FCSTD DOCUMENT  (FreeCAD 0.16R6706 (Git))
Label: femur
License: All rights reserved
LicenseURL: http://en.wikipedia.org/wiki/All_rights_reserved
objects: Sketcher::SketchObject×3
note: 3 computed .brp shape members not serialized (recipe doc carries the construction recipe); baked Part::Feature solids carry a one-line shape summary decoded from their .brp

FEATURE [Sketcher::SketchObject] Sketch003  label="femur_down"
  sketch-geometry (38):
    g0: LineSegment [constr] StartX=-11.4129 StartY=31.5472 StartZ=0 EndX=48.5871 EndY=31.5472 EndZ=0
    g1: GeomPoint [constr] X=-11.4129 Y=31.5472 Z=0
    g2: GeomPoint [constr] X=48.5871 Y=31.5472 Z=0
    g3: GeomPoint [constr] X=18.5871 Y=31.5472 Z=0
    g4: LineSegment [constr] StartX=18.5871 StartY=37.0472 StartZ=0 EndX=18.5871 EndY=26.0472 EndZ=0
    g5: LineSegment [constr] StartX=-11.4129 StartY=37.0472 StartZ=0 EndX=48.5871 EndY=37.0472 EndZ=0
    g6: LineSegment [constr] StartX=-11.4129 StartY=26.0472 StartZ=0 EndX=48.5871 EndY=26.0472 EndZ=0
    g7: Circle CenterX=48.5871 CenterY=31.5472 CenterZ=0 NormalX=0 NormalY=0 NormalZ=1 Radius=1.5
    g8: Circle CenterX=-11.4129 CenterY=31.5472 CenterZ=0 NormalX=0 NormalY=0 NormalZ=1 Radius=1.5
    g9: ArcOfCircle CenterX=48.5871 CenterY=31.5472 CenterZ=0 NormalX=0 NormalY=0 NormalZ=1 Radius=5.5 StartAngle=4.71238 EndAngle=7.85399
    g10: ArcOfCircle CenterX=-11.4129 CenterY=31.5472 CenterZ=0 NormalX=0 NormalY=0 NormalZ=1 Radius=5.5 StartAngle=1.57079 EndAngle=4.71239
    g11: LineSegment StartX=48.5871 StartY=37.0472 StartZ=0 EndX=25.858 EndY=37.0472 EndZ=0
    g12: LineSegment [constr] StartX=22.1954 StartY=37.0472 StartZ=0 EndX=29.3838 EndY=26.7835 EndZ=0
    g13: LineSegment StartX=33.5621 StartY=26.0472 StartZ=0 EndX=31.8411 EndY=28.5045 EndZ=0
    g14: LineSegment StartX=29.3838 StartY=26.7835 StartZ=0 EndX=31.8411 EndY=28.5045 EndZ=0
    g15: LineSegment StartX=48.5871 StartY=26.0472 StartZ=0 EndX=33.5621 EndY=26.0472 EndZ=0
    g16: GeomPoint [constr] X=22.1954 Y=37.0472 Z=0
    g17: LineSegment StartX=23.9164 StartY=34.5899 StartZ=0 EndX=26.3737 EndY=36.3109 EndZ=0
    g18: LineSegment StartX=-11.4129 StartY=26.0472 StartZ=0 EndX=3.61207 EndY=26.0472 EndZ=0
    g19: LineSegment StartX=29.3838 StartY=26.7835 StartZ=0 EndX=29.8995 EndY=26.0472 EndZ=0
    g20: LineSegment StartX=26.3737 StartY=36.3109 StartZ=0 EndX=25.858 EndY=37.0472 EndZ=0
    g21: LineSegment [constr] StartX=14.9788 StartY=37.0472 StartZ=0 EndX=7.27468 EndY=26.0472 EndZ=0
    g22: LineSegment StartX=13.2578 StartY=34.5899 StartZ=0 EndX=10.8005 EndY=36.3109 EndZ=0
    g23: LineSegment StartX=10.8005 StartY=36.3109 StartZ=0 EndX=11.3162 EndY=37.0472 EndZ=0
    g24: LineSegment StartX=-11.4129 StartY=37.0472 StartZ=0 EndX=11.3162 EndY=37.0472 EndZ=0
    g25: LineSegment StartX=7.27468 StartY=26.0472 StartZ=0 EndX=7.79034 EndY=26.7835 EndZ=0
    g26: LineSegment StartX=7.79034 StartY=26.7835 StartZ=0 EndX=5.33307 EndY=28.5045 EndZ=0
    g27: LineSegment StartX=5.33307 StartY=28.5045 StartZ=0 EndX=3.61207 EndY=26.0472 EndZ=0
    g28: LineSegment StartX=29.8995 StartY=26.0472 StartZ=0 EndX=7.27468 EndY=26.0472 EndZ=0
    g29: LineSegment StartX=23.9164 StartY=34.5899 StartZ=0 EndX=22.1954 EndY=37.0472 EndZ=0
    g30: LineSegment StartX=13.2578 StartY=34.5899 StartZ=0 EndX=14.9788 EndY=37.0472 EndZ=0
    g31: LineSegment StartX=14.9788 StartY=37.0472 StartZ=0 EndX=22.1954 EndY=37.0472 EndZ=0
    g32: LineSegment [constr] StartX=22.1954 StartY=37.0472 StartZ=0 EndX=24.6527 EndY=38.7682 EndZ=0
    g33: LineSegment [constr] StartX=25.858 StartY=37.0472 StartZ=0 EndX=24.6527 EndY=38.7682 EndZ=0
    g34: LineSegment [constr] StartX=14.9788 StartY=37.0472 StartZ=0 EndX=12.5215 EndY=38.7682 EndZ=0
    g35: LineSegment [constr] StartX=11.3162 StartY=37.0472 StartZ=0 EndX=12.5215 EndY=38.7682 EndZ=0
    g36: Circle CenterX=18.5871 CenterY=31.5472 CenterZ=0 NormalX=0 NormalY=0 NormalZ=1 Radius=1.2
    g37: LineSegment [constr] StartX=18.5871 StartY=34.5899 StartZ=0 EndX=18.5871 EndY=26.7835 EndZ=0
  constraints (99):
    c: PointOnObject(g1,g0)
    c: PointOnObject(g2,g0)
    c: Symmetric(g1,g2,g3)
    c: Distance(g3,g2) = 30
    c: Vertical(g4)
    c: Symmetric(g4,g4,g3)
    c: Distance(g3,g4) = 5.5
    c: Horizontal(g5)
    c: PointOnObject(g4,g5)
    c: Horizontal(g6)
    c: PointOnObject(g4,g6)
    c: Coincident(g7,g2)
    c: Radius(g7) = 1.5
    c: Coincident(g8,g1)
    c: Radius(g8) = 1.5
    c: Coincident(g9,g2)
    c: Coincident(g9,g6)
    c: Coincident(g5,g9)
    c: Tangent(g9,g5)
    c: Coincident(g10,g1)
    c: Coincident(g10,g6)
    c: Tangent(g6,g10)
    c: Coincident(g5,g10)
    c: Coincident(g11,g5)
    c: Coincident(g0,g2)
    c: Coincident(g0,g1)
    c: PointOnObject(g14,g12)
    c: Distance(g13,g13) = 3
    c: Coincident(g14,g13)
    c: Coincident(g15,g6)
    c: Perpendicular(g14,g12)
    c: Perpendicular(g14,g13)
    c: Distance(g13,g12) = 3
    c: PointOnObject(g17,g12)
    c: Distance(g17,g16) = 3
    c: Distance(g17,g17) = 3
    c: Perpendicular(g12,g17)
    c: PointOnObject(g12,g14)
    c: Coincident(g18,g6)
    c: PointOnObject(g13,g6)
    c: Coincident(g15,g13)
    c: Coincident(g19,g12)
    c: PointOnObject(g19,g6)
    c: Perpendicular(g14,g19)
    c: Coincident(g20,g17)
    c: PointOnObject(g20,g5)
    c: Perpendicular(g17,g20)
    c: Coincident(g11,g20)
    c: PointOnObject(g21,g6)
    c: PointOnObject(g22,g21)
    c: Distance(g22,g21) = 3
    c: Distance(g22,g22) = 3
    c: Perpendicular(g21,g22)
    c: Coincident(g23,g22)
    c: PointOnObject(g23,g5)
    c: Perpendicular(g22,g23)
    c: Coincident(g24,g5)
    c: Coincident(g23,g24)
    c: Coincident(g25,g21)
    c: PointOnObject(g25,g21)
    c: Coincident(g26,g25)
    c: Distance(g26,g25) = 3
    c: Coincident(g27,g26)
    c: PointOnObject(g27,g6)
    c: Distance(g27,g26) = 3
    c: Perpendicular(g26,g27)
    c: Perpendicular(g21,g26)
    c: Coincident(g18,g27)
    c: Coincident(g28,g19)
    c: Coincident(g21,g28)
    c: Coincident(g29,g12)
    c: Coincident(g17,g29)
    c: Coincident(g16,g12)
    c: PointOnObject(g12,g5)
    c: PointOnObject(g21,g5)
    c: Coincident(g30,g22)
    c: Coincident(g21,g30)
    c: Coincident(g31,g21)
    c: Coincident(g12,g31)
    c: Distance(g13,g0) = 16
    c: Tangent(g6,g9)
    c: Coincident(g32,g12)
    c: Perpendicular(g32,g12)
    c: Coincident(g33,g11)
    c: Parallel(g20,g33)
    c: Coincident(g32,g33)
    c: Distance(g32,g0) = 25
    c: Coincident(g34,g21)
    c: Perpendicular(g21,g34)
    c: Coincident(g35,g23)
    c: Parallel(g35,g23)
    c: Coincident(g34,g35)
    c: Distance(g18,g0) = 16
    c: Distance(g34,g0) = 25
    c: Radius(g36) = 1.2
    c: Symmetric(g25,g12,g37)
    c: Symmetric(g22,g17,g37)
    c: PointOnObject(g36,g37)
    c: PointOnObject(g36,g0)
FEATURE [Sketcher::SketchObject] Sketch004  label="femur_up"
  sketch-geometry (52):
    g0: LineSegment [constr] StartX=-9.22309 StartY=9.62854 StartZ=0 EndX=50.7769 EndY=9.62854 EndZ=0
    g1: GeomPoint [constr] X=-9.22309 Y=9.62854 Z=0
    g2: GeomPoint [constr] X=50.7769 Y=9.62854 Z=0
    g3: GeomPoint [constr] X=20.7769 Y=9.62854 Z=0
    g4: LineSegment [constr] StartX=20.7769 StartY=15.1285 StartZ=0 EndX=20.7769 EndY=4.12854 EndZ=0
    g5: LineSegment [constr] StartX=-9.22309 StartY=15.1285 StartZ=0 EndX=50.7769 EndY=15.1285 EndZ=0
    g6: LineSegment [constr] StartX=-9.22309 StartY=4.12854 StartZ=0 EndX=50.7769 EndY=4.12854 EndZ=0
    g7: Circle CenterX=50.7769 CenterY=9.62854 CenterZ=0 NormalX=0 NormalY=0 NormalZ=1 Radius=3.5
    g8: Circle CenterX=-9.22309 CenterY=9.62854 CenterZ=0 NormalX=0 NormalY=0 NormalZ=1 Radius=3.5
    g9: LineSegment StartX=50.7769 StartY=15.1285 StartZ=0 EndX=28.0478 EndY=15.1285 EndZ=0
    g10: LineSegment [constr] StartX=24.3852 StartY=15.1285 StartZ=0 EndX=31.5737 EndY=4.8648 EndZ=0
    g11: LineSegment StartX=35.7519 StartY=4.12854 StartZ=0 EndX=34.0309 EndY=6.5858 EndZ=0
    g12: LineSegment StartX=31.5737 StartY=4.8648 StartZ=0 EndX=34.0309 EndY=6.5858 EndZ=0
    g13: LineSegment StartX=50.7769 StartY=4.12854 StartZ=0 EndX=35.7519 EndY=4.12854 EndZ=0
    g14: GeomPoint [constr] X=24.3852 Y=15.1285 Z=0
    g15: LineSegment StartX=26.1062 StartY=12.6713 StartZ=0 EndX=28.5635 EndY=14.3923 EndZ=0
    g16: LineSegment StartX=-9.22309 StartY=4.12854 StartZ=0 EndX=5.80189 EndY=4.12854 EndZ=0
    g17: LineSegment StartX=31.5737 StartY=4.8648 StartZ=0 EndX=32.0893 EndY=4.12854 EndZ=0
    g18: LineSegment StartX=28.5635 StartY=14.3923 StartZ=0 EndX=28.0478 EndY=15.1285 EndZ=0
    g19: LineSegment [constr] StartX=17.1686 StartY=15.1285 StartZ=0 EndX=9.4645 EndY=4.12854 EndZ=0
    g20: LineSegment StartX=15.4476 StartY=12.6713 StartZ=0 EndX=12.9903 EndY=14.3923 EndZ=0
    g21: LineSegment StartX=12.9903 StartY=14.3923 StartZ=0 EndX=13.506 EndY=15.1285 EndZ=0
    g22: LineSegment StartX=-9.22309 StartY=15.1285 StartZ=0 EndX=13.506 EndY=15.1285 EndZ=0
    g23: LineSegment StartX=9.4645 StartY=4.12854 StartZ=0 EndX=9.98015 EndY=4.8648 EndZ=0
    g24: LineSegment StartX=9.98015 StartY=4.8648 StartZ=0 EndX=7.52289 EndY=6.5858 EndZ=0
    g25: LineSegment StartX=7.52289 StartY=6.5858 StartZ=0 EndX=5.80189 EndY=4.12854 EndZ=0
    g26: LineSegment StartX=32.0893 StartY=4.12854 StartZ=0 EndX=9.4645 EndY=4.12854 EndZ=0
    g27: LineSegment StartX=26.1062 StartY=12.6713 StartZ=0 EndX=24.3852 EndY=15.1285 EndZ=0
    g28: LineSegment StartX=15.4476 StartY=12.6713 StartZ=0 EndX=17.1686 EndY=15.1285 EndZ=0
    g29: LineSegment StartX=17.1686 StartY=15.1285 StartZ=0 EndX=24.3852 EndY=15.1285 EndZ=0
    g30: LineSegment [constr] StartX=24.3852 StartY=15.1285 StartZ=0 EndX=26.8425 EndY=16.8495 EndZ=0
    g31: LineSegment [constr] StartX=28.0478 StartY=15.1285 StartZ=0 EndX=26.8425 EndY=16.8495 EndZ=0
    g32: LineSegment [constr] StartX=17.1686 StartY=15.1285 StartZ=0 EndX=14.7113 EndY=16.8495 EndZ=0
    g33: LineSegment [constr] StartX=13.506 StartY=15.1285 StartZ=0 EndX=14.7113 EndY=16.8495 EndZ=0
    g34: Circle CenterX=20.7769 CenterY=9.62854 CenterZ=0 NormalX=0 NormalY=0 NormalZ=1 Radius=1.5
    g35: LineSegment [constr] StartX=20.7769 StartY=12.6713 StartZ=0 EndX=20.7769 EndY=4.8648 EndZ=0
    g36: LineSegment [constr] StartX=50.7769 StartY=15.1285 StartZ=0 EndX=50.7769 EndY=4.12854 EndZ=0
    g37: LineSegment [constr] StartX=-9.22309 StartY=15.1285 StartZ=0 EndX=-9.22309 EndY=4.12854 EndZ=0
    g38: Circle CenterX=43.7769 CenterY=9.62854 CenterZ=0 NormalX=0 NormalY=0 NormalZ=1 Radius=1.2
    g39: Circle CenterX=-2.22309 CenterY=9.62854 CenterZ=0 NormalX=0 NormalY=0 NormalZ=1 Radius=1.2
    g40: Circle CenterX=57.7769 CenterY=9.62854 CenterZ=0 NormalX=0 NormalY=0 NormalZ=1 Radius=1.2
    g41: Circle CenterX=-16.2231 CenterY=9.62854 CenterZ=0 NormalX=0 NormalY=0 NormalZ=1 Radius=1.2
    g42: ArcOfEllipse CenterX=50.7769 CenterY=9.62854 CenterZ=0 NormalX=0 NormalY=0 NormalZ=1 MajorRadius=11 MinorRadius=5.5 AngleXU=0 StartAngle=4.71239 EndAngle=7.85398
    g43: LineSegment [constr] StartX=61.7769 StartY=9.62854 StartZ=0 EndX=39.7769 EndY=9.62854 EndZ=0
    g44: LineSegment [constr] StartX=50.7769 StartY=15.1285 StartZ=0 EndX=50.7769 EndY=4.12854 EndZ=0
    g45: GeomPoint [constr] X=60.3032 Y=9.62854 Z=0
    g46: GeomPoint [constr] X=41.2506 Y=9.62854 Z=0
    g47: ArcOfEllipse CenterX=-9.22309 CenterY=9.62854 CenterZ=0 NormalX=0 NormalY=0 NormalZ=1 MajorRadius=11 MinorRadius=5.5 AngleXU=0 StartAngle=1.5708 EndAngle=4.71239
    g48: LineSegment [constr] StartX=1.77691 StartY=9.62854 StartZ=0 EndX=-20.2231 EndY=9.62854 EndZ=0
    g49: LineSegment [constr] StartX=-9.22309 StartY=15.1285 StartZ=0 EndX=-9.22309 EndY=4.12854 EndZ=0
    g50: GeomPoint [constr] X=0.303187 Y=9.62854 Z=0
    g51: GeomPoint [constr] X=-18.7494 Y=9.62854 Z=0
  constraints (123):
    c: PointOnObject(g1,g0)
    c: PointOnObject(g2,g0)
    c: Symmetric(g1,g2,g3)
    c: Distance(g3,g2) = 30
    c: Vertical(g4)
    c: Symmetric(g4,g4,g3)
    c: Distance(g3,g4) = 5.5
    c: Horizontal(g5)
    c: PointOnObject(g4,g5)
    c: Horizontal(g6)
    c: PointOnObject(g4,g6)
    c: Coincident(g7,g2)
    c: Radius(g7) = 3.5
    c: Coincident(g8,g1)
    c: Radius(g8) = 3.5
    c: Coincident(g9,g5)
    c: Coincident(g0,g2)
    c: Coincident(g0,g1)
    c: PointOnObject(g12,g10)
    c: Distance(g11,g11) = 3
    c: Coincident(g12,g11)
    c: Coincident(g13,g6)
    c: Perpendicular(g12,g10)
    c: Perpendicular(g12,g11)
    c: Distance(g11,g10) = 3
    c: PointOnObject(g15,g10)
    c: Distance(g15,g14) = 3
    c: Distance(g15,g15) = 3
    c: Perpendicular(g10,g15)
    c: PointOnObject(g10,g12)
    c: Coincident(g16,g6)
    c: PointOnObject(g11,g6)
    c: Coincident(g13,g11)
    c: Coincident(g17,g10)
    c: PointOnObject(g17,g6)
    c: Perpendicular(g12,g17)
    c: Coincident(g18,g15)
    c: PointOnObject(g18,g5)
    c: Perpendicular(g15,g18)
    c: Coincident(g9,g18)
    c: PointOnObject(g19,g6)
    c: PointOnObject(g20,g19)
    c: Distance(g20,g19) = 3
    c: Distance(g20,g20) = 3
    c: Perpendicular(g19,g20)
    c: Coincident(g21,g20)
    c: PointOnObject(g21,g5)
    c: Perpendicular(g20,g21)
    c: Coincident(g22,g5)
    c: Coincident(g21,g22)
    c: Coincident(g23,g19)
    c: PointOnObject(g23,g19)
    c: Coincident(g24,g23)
    c: Distance(g24,g23) = 3
    c: Coincident(g25,g24)
    c: PointOnObject(g25,g6)
    c: Distance(g25,g24) = 3
    c: Perpendicular(g24,g25)
    c: Perpendicular(g19,g24)
    c: Coincident(g16,g25)
    c: Coincident(g26,g17)
    c: Coincident(g19,g26)
    c: Coincident(g27,g10)
    c: Coincident(g15,g27)
    c: Coincident(g14,g10)
    c: PointOnObject(g10,g5)
    c: PointOnObject(g19,g5)
    c: Coincident(g28,g20)
    c: Coincident(g19,g28)
    c: Coincident(g29,g19)
    c: Coincident(g10,g29)
    c: Distance(g11,g0) = 16
    c: Coincident(g30,g10)
    c: Perpendicular(g30,g10)
    c: Coincident(g31,g9)
    c: Parallel(g18,g31)
    c: Coincident(g30,g31)
    c: Distance(g30,g0) = 25
    c: Coincident(g32,g19)
    c: Perpendicular(g19,g32)
    c: Coincident(g33,g21)
    c: Parallel(g33,g21)
    c: Coincident(g32,g33)
    c: Distance(g16,g0) = 16
    c: Distance(g32,g0) = 25
    c: Radius(g34) = 1.5
    c: Symmetric(g23,g10,g35)
    c: Symmetric(g20,g15,g35)
    c: PointOnObject(g34,g35)
    c: Coincident(g36,g5)
    c: Coincident(g36,g6)
    c: Vertical(g36)
    c: Coincident(g37,g5)
    c: Coincident(g37,g6)
    c: Vertical(g37)
    c: PointOnObject(g0,g36)
    c: Distance(g0,g6) = 5.5
    c: PointOnObject(g0,g37)
    c: PointOnObject(g38,g0)
    c: Radius(g38) = 1.2
    c: Distance(g0,g38) = 7
    c: PointOnObject(g39,g0)
    c: Radius(g39) = 1.2
    c: Distance(g0,g39) = 7
    c: Radius(g40) = 1.2
    c: PointOnObject(g40,g0)
    c: Distance(g0,g40) = 7
    c: Radius(g41) = 1.2
    c: PointOnObject(g41,g0)
    c: Distance(g41,g0) = 7
    c: InternalAlignment(g43-g46 -> g42) x4
    c: Coincident(g42,g0)
    c: Coincident(g5,g44)
    c: PointOnObject(g42,g36)
    c: PointOnObject(g42,g36)
    c: InternalAlignment(g48-g51 -> g47) x4
    c: Coincident(g47,g0)
    c: Coincident(g6,g49)
    c: PointOnObject(g47,g37)
    c: PointOnObject(g47,g37)
    c: Distance(g40,g43) = 4
    c: Distance(g48,g41) = 4
    c: PointOnObject(g34,g0)
FEATURE [Sketcher::SketchObject] Sketch005  label="femur_joint"
  sketch-geometry (16):
    g0: LineSegment [constr] StartX=4.47065 StartY=61.2395 StartZ=0 EndX=33.9706 EndY=61.2395 EndZ=0
    g1: LineSegment [constr] StartX=33.9706 StartY=61.2395 StartZ=0 EndX=33.9706 EndY=45.7095 EndZ=0
    g2: LineSegment [constr] StartX=33.9706 StartY=45.7095 StartZ=0 EndX=4.47065 EndY=45.7095 EndZ=0
    g3: LineSegment [constr] StartX=4.47065 StartY=45.7095 StartZ=0 EndX=4.47065 EndY=61.2395 EndZ=0
    g4: LineSegment StartX=1.47065 StartY=61.2395 StartZ=0 EndX=36.9706 EndY=61.2395 EndZ=0
    g5: LineSegment StartX=1.47065 StartY=45.7095 StartZ=0 EndX=36.9706 EndY=45.7095 EndZ=0
    g6: LineSegment StartX=36.9706 StartY=61.2395 StartZ=0 EndX=36.9706 EndY=58.2395 EndZ=0
    g7: LineSegment StartX=36.9706 StartY=45.7095 StartZ=0 EndX=36.9706 EndY=48.7095 EndZ=0
    g8: LineSegment StartX=36.9706 StartY=58.2395 StartZ=0 EndX=33.9706 EndY=58.2395 EndZ=0
    g9: LineSegment StartX=36.9706 StartY=48.7095 StartZ=0 EndX=33.9706 EndY=48.7095 EndZ=0
    g10: LineSegment StartX=33.9706 StartY=58.2395 StartZ=0 EndX=33.9706 EndY=48.7095 EndZ=0
    g11: LineSegment StartX=1.47065 StartY=61.2395 StartZ=0 EndX=1.47065 EndY=58.2395 EndZ=0
    g12: LineSegment StartX=1.47065 StartY=45.7095 StartZ=0 EndX=1.47065 EndY=48.7095 EndZ=0
    g13: LineSegment StartX=1.47065 StartY=48.7095 StartZ=0 EndX=4.47065 EndY=48.7095 EndZ=0
    g14: LineSegment StartX=1.47065 StartY=58.2395 StartZ=0 EndX=4.47065 EndY=58.2395 EndZ=0
    g15: LineSegment StartX=4.47065 StartY=58.2395 StartZ=0 EndX=4.47065 EndY=48.7095 EndZ=0
  constraints (46):
    c: Coincident(g0,g1)
    c: Coincident(g1,g2)
    c: Coincident(g2,g3)
    c: Coincident(g3,g0)
    c: Horizontal(g0)
    c: Horizontal(g2)
    c: Vertical(g1)
    c: Vertical(g3)
    c: Distance(g0,g3) = 29.5
    c: Distance(g1,g0) = 15.53
    c: PointOnObject(g0,g4)
    c: Distance(g4,g1) = 3
    c: Distance(g4,g3) = 3
    c: Horizontal(g5)
    c: PointOnObject(g1,g5)
    c: Horizontal(g4)
    c: Distance(g5,g3) = 3
    c: Distance(g5,g1) = 3
    c: Coincident(g6,g4)
    c: Coincident(g7,g5)
    c: Distance(g5,g7) = 3
    c: Distance(g6,g4) = 3
    c: Perpendicular(g5,g7)
    c: Perpendicular(g6,g4)
    c: Coincident(g8,g6)
    c: PointOnObject(g8,g1)
    c: Perpendicular(g1,g8)
    c: Coincident(g9,g7)
    c: PointOnObject(g9,g1)
    c: Perpendicular(g1,g9)
    c: Coincident(g10,g8)
    c: Coincident(g9,g10)
    c: Coincident(g11,g4)
    c: Coincident(g12,g5)
    c: Coincident(g13,g12)
    c: PointOnObject(g13,g3)
    c: PointOnObject(g14,g3)
    c: Distance(g14) = 3
    c: Coincident(g11,g14)
    c: Distance(g11,g4) = 3
    c: Distance(g12,g13) = 3
    c: Distance(g12,g5) = 3
    c: Perpendicular(g5,g12)
    c: Perpendicular(g4,g11)
    c: Coincident(g15,g14)
    c: Coincident(g13,g15)
